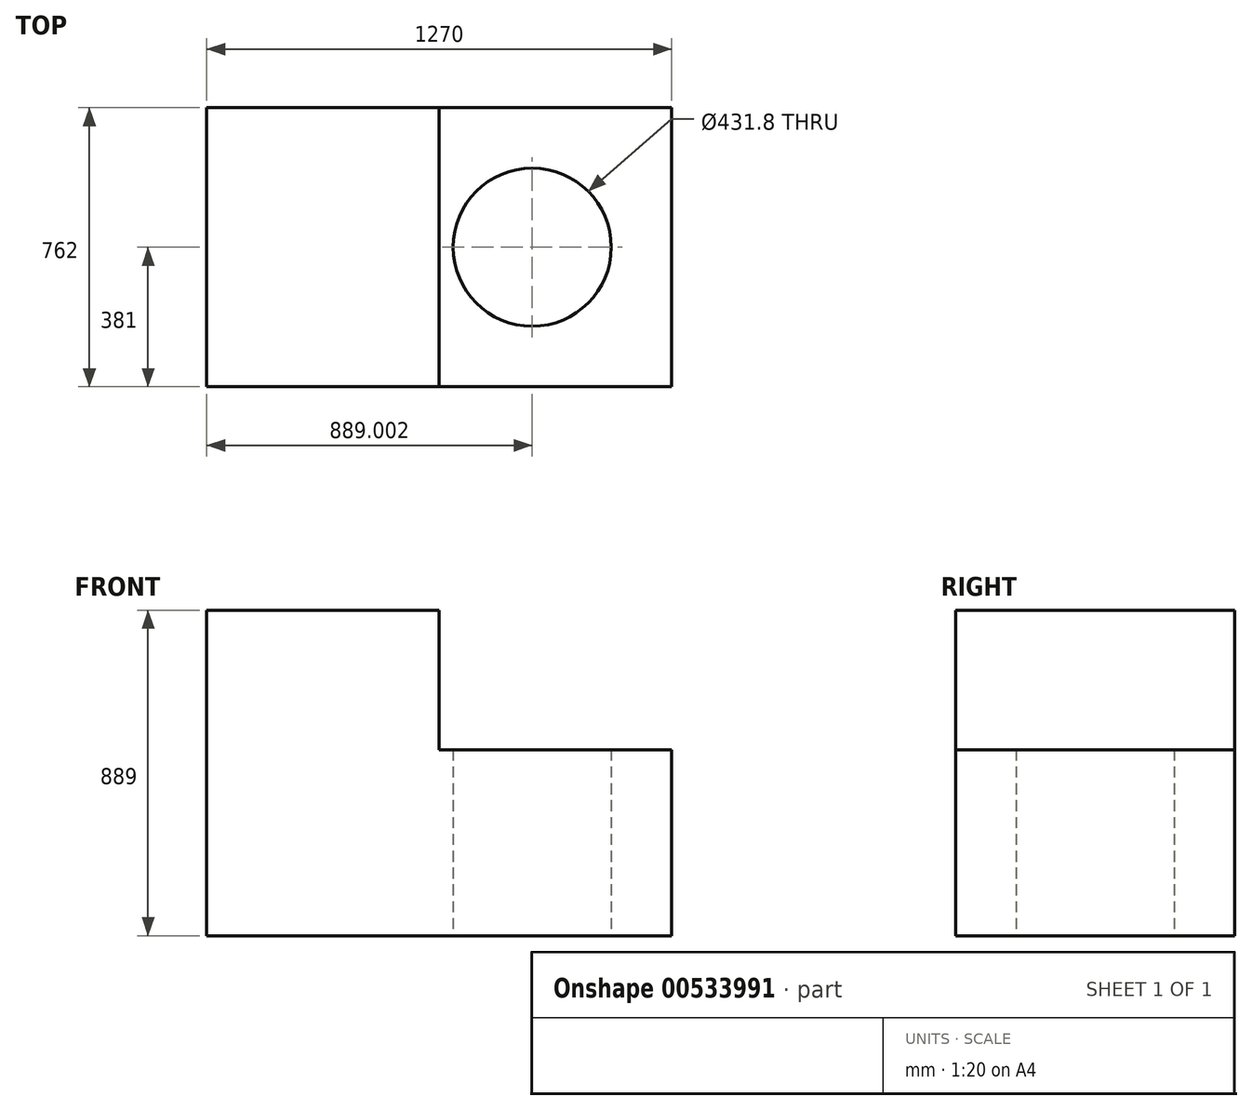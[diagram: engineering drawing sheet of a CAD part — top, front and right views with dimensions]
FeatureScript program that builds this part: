
annotation { "Feature Type Name" : "Feature", "Feature Type Description" : "" }
export const myFeature = defineFeature(function(context is Context, id is Id, definition is map)
    precondition{}
    {
        {
            var Q0;
            Q0=qCreatedBy(makeId("Front.planeOp"),FACE);
            var sketch = newSketch(context, id + "F0", { "sketchPlane" : qUnion([Q0])});
            skLineSegment(sketch, "E0", {"start": v(-633.14, -431.6) * mm, "end": v(636.86, -431.6) * mm});
            skLineSegment(sketch, "E1", {"start": v(-633.14, -431.6) * mm, "end": v(-633.14, 457.4) * mm});
            skLineSegment(sketch, "E2", {"start": v(-633.14, 457.4) * mm, "end": v(1.86, 457.4) * mm});
            skLineSegment(sketch, "E3", {"start": v(636.86, -431.6) * mm, "end": v(636.86, 76.4) * mm});
            skLineSegment(sketch, "E4", {"start": v(636.86, 76.4) * mm, "end": v(1.86, 76.4) * mm});
            skLineSegment(sketch, "E5", {"start": v(1.86, 76.4) * mm, "end": v(1.86, 457.4) * mm});
            skSolve(sketch);
        }
        {
            var Q0;
            Q0=makeQuery(id+"F0.imprint","IMPRINT",FACE,{"disambiguationData":[TD([[makeQuery(id+"F0.imprint","IMPRINT",EDGE,{"derivedFrom":sQuery(id+"F0.wireOp",EDGE,"E0")}),1.0]])]});
            var sketch = newSketch(context, id + "F1", { "sketchPlane" : qUnion([Q0])});
            skSolve(sketch);
        }
        {
            var Q0;
            Q0 = qSketchRegion(id + "F0", true);
            extrude(context, id + "F2", {"entities" : qUnion([Q0]), "depth" : 381 * mm, "offsetDistance" : 25.4 * mm});
        }
        {
            var Q0;
            Q0=makeQuery(id+"F2.opExtrude","SWEPT_BODY",BODY,{"disambiguationData":[OSD([sQuery(id+"F0.wireOp",EDGE,"E0"),sQuery(id+"F0.wireOp",EDGE,"E1"),sQuery(id+"F0.wireOp",EDGE,"E2"),sQuery(id+"F0.wireOp",EDGE,"E3"),sQuery(id+"F0.wireOp",EDGE,"E4"),sQuery(id+"F0.wireOp",EDGE,"E5")])]});
            var Q1;
            Q1=makeQuery(id+"F1.imprint","IMPRINT",FACE,{"disambiguationData":[TD([[makeQuery(id+"F1.imprint","IMPRINT",EDGE,{"derivedFrom":makeQuery(id+"F0.imprint","IMPRINT",EDGE,{"derivedFrom":sQuery(id+"F0.wireOp",EDGE,"E0")})}),1.0]])]});
            mirror(context, id + "F3", {"operationType" : NewBodyOperationType.ADD, "entities" : qUnion([Q0]), "mirrorPlane" : qUnion([Q1])});
        }
        {
            var Q0;
            {var subQ0=makeQuery(id+"F2.opExtrude","SWEPT_FACE",FACE,{"disambiguationData":[OSD([sQuery(id+"F0.wireOp",EDGE,"E0")])]});Q0=makeQuery(id+"F3.boolean.opBoolean","MERGE",FACE,{"derivedFrom":[subQ0,makeQuery(id+"F3.opPattern","COPY",FACE,{"derivedFrom":subQ0,"instanceName":"1"})]});}
            var sketch = newSketch(context, id + "F4", { "sketchPlane" : qUnion([Q0])});
            skPoint(sketch, "E6.endSnap0", {"position": v(-633.14, 0) * mm});
            skCircle(sketch, "E7", {"center": v(255.86, 0) * mm, "radius": 215.9 * mm});
            skSolve(sketch);
        }
        {
            var Q0;
            Q0=makeQuery(id+"F4.imprint","IMPRINT",FACE,{"disambiguationData":[TD([[makeQuery(id+"F4.imprint","IMPRINT",EDGE,{"derivedFrom":sQuery(id+"F4.wireOp",EDGE,"E7")}),1.0]])]});
            var Q1;
            Q1=sQuery(id+"F4.wireOp",EDGE,"E7");
            extrude(context, id + "F5", {"entities" : qUnion([Q0]), "operationType" : NewBodyOperationType.REMOVE, "surfaceEntities" : qUnion([Q1]), "endBound" : BoundingType.UP_TO_NEXT, "oppositeDirection" : true, "depth" : 25.4 * mm, "offsetDistance" : 25.4 * mm});
        }
    });
